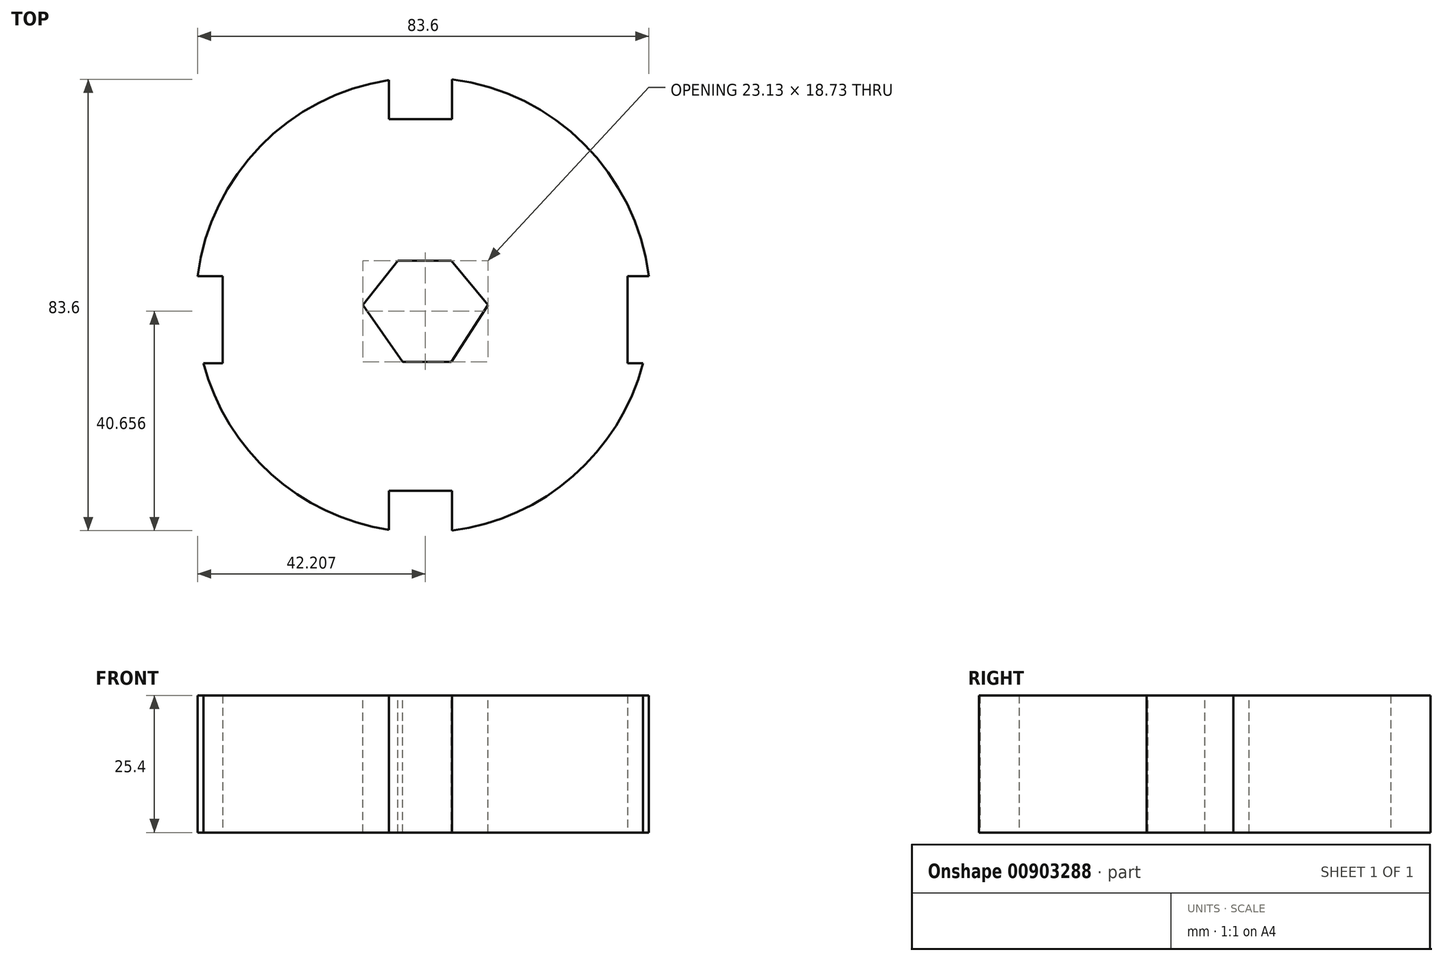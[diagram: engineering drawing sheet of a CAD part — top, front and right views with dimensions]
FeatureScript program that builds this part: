
annotation { "Feature Type Name" : "Feature", "Feature Type Description" : "" }
export const myFeature = defineFeature(function(context is Context, id is Id, definition is map)
    precondition{}
    {
        {
            var Q0;
            Q0=qCreatedBy(makeId("Top.planeOp"),FACE);
            var sketch = newSketch(context, id + "F0", { "sketchPlane" : qUnion([Q0])});
            skCircle(sketch, "E0", {"center": v(0, 0) * mm, "radius": 42.14 * mm});
            skLineSegment(sketch, "E1.bottom", {"start": v(-46.4, 5.32) * mm, "end": v(-37.16, 5.32) * mm});
            skLineSegment(sketch, "E1.top", {"start": v(-46.4, -10.79) * mm, "end": v(-37.16, -10.79) * mm});
            skLineSegment(sketch, "E1.left", {"start": v(-46.4, 5.32) * mm, "end": v(-46.4, -10.79) * mm});
            skLineSegment(sketch, "E1.right", {"start": v(-37.16, 5.32) * mm, "end": v(-37.16, -10.79) * mm});
            skLineSegment(sketch, "E2.bottom", {"start": v(37.87, 5.32) * mm, "end": v(47.11, 5.32) * mm});
            skLineSegment(sketch, "E2.top", {"start": v(37.87, -10.79) * mm, "end": v(47.11, -10.79) * mm});
            skLineSegment(sketch, "E2.left", {"start": v(37.87, 5.32) * mm, "end": v(37.87, -10.79) * mm});
            skLineSegment(sketch, "E2.right", {"start": v(47.11, 5.32) * mm, "end": v(47.11, -10.79) * mm});
            skLineSegment(sketch, "E3", {"start": v(0, 42.14) * mm, "end": v(0, -42.14) * mm, "construction": true});
            skLineSegment(sketch, "E4.MirrorCS", {"start": v(-46.4, -10.79) * mm, "end": v(-46.4, 5.32) * mm});
            skLineSegment(sketch, "E5.bottom", {"start": v(-6.34, 46.75) * mm, "end": v(5.3, 46.75) * mm});
            skLineSegment(sketch, "E5.top", {"start": v(-6.34, 34.42) * mm, "end": v(5.3, 34.42) * mm});
            skLineSegment(sketch, "E5.left", {"start": v(-6.34, 46.75) * mm, "end": v(-6.34, 34.42) * mm});
            skLineSegment(sketch, "E5.right", {"start": v(5.3, 46.75) * mm, "end": v(5.3, 34.42) * mm});
            skLineSegment(sketch, "E6", {"start": v(-42.14, 0) * mm, "end": v(42.14, 0) * mm, "construction": true});
            skLineSegment(sketch, "E7.MirrorCS", {"start": v(-6.34, -34.42) * mm, "end": v(5.3, -34.42) * mm});
            skLineSegment(sketch, "E8.MirrorCS", {"start": v(-6.34, -46.75) * mm, "end": v(-6.34, -34.42) * mm});
            skLineSegment(sketch, "E9.MirrorCS", {"start": v(-6.34, -46.75) * mm, "end": v(5.3, -46.75) * mm});
            skLineSegment(sketch, "E10.MirrorCS", {"start": v(5.3, -46.75) * mm, "end": v(5.3, -34.42) * mm});
            skSolve(sketch);
        }
        {
            var Q0;
            {var subQ0=sQuery(id+"F0.wireOp",EDGE,"E1.right");Q0=makeQuery(id+"F0.imprint","IMPRINT",FACE,{"disambiguationData":[TD([[makeQuery(id+"F0.imprint","IMPRINT",EDGE,{"derivedFrom":subQ0}),1.0]])]});}
            extrude(context, id + "F1", {"entities" : qUnion([Q0]), "depth" : 25.4 * mm, "offsetDistance" : 25.4 * mm});
        }
        {
            var Q0;
            Q0=makeQuery(id+"F1.opExtrude","CAP_FACE",FACE,{"disambiguationData":[OSD([sQuery(id+"F0.wireOp",EDGE,"E0"),sQuery(id+"F0.wireOp",EDGE,"E1.bottom"),sQuery(id+"F0.wireOp",EDGE,"E1.top"),sQuery(id+"F0.wireOp",EDGE,"E1.right"),sQuery(id+"F0.wireOp",EDGE,"E2.bottom"),sQuery(id+"F0.wireOp",EDGE,"E2.top"),sQuery(id+"F0.wireOp",EDGE,"E2.left"),sQuery(id+"F0.wireOp",EDGE,"E5.top"),sQuery(id+"F0.wireOp",EDGE,"E5.left"),sQuery(id+"F0.wireOp",EDGE,"E5.right"),sQuery(id+"F0.wireOp",EDGE,"E7.MirrorCS"),sQuery(id+"F0.wireOp",EDGE,"E8.MirrorCS"),sQuery(id+"F0.wireOp",EDGE,"E10.MirrorCS")])],"isStart":false});
            var sketch = newSketch(context, id + "F2", { "sketchPlane" : qUnion([Q0])});
            skLineSegment(sketch, "E11", {"start": v(-11.16, 0) * mm, "end": v(-4.73, 8.22) * mm});
            skLineSegment(sketch, "E12", {"start": v(-4.73, 8.22) * mm, "end": v(5.22, 8.22) * mm});
            skLineSegment(sketch, "E13", {"start": v(5.22, 8.22) * mm, "end": v(11.97, 0) * mm});
            skLineSegment(sketch, "E14", {"start": v(11.97, 0) * mm, "end": v(5.22, -10.51) * mm});
            skLineSegment(sketch, "E15", {"start": v(5.22, -10.51) * mm, "end": v(-3.8, -10.51) * mm});
            skLineSegment(sketch, "E16", {"start": v(-3.8, -10.51) * mm, "end": v(-11.16, 0) * mm});
            skSolve(sketch);
        }
        {
            var Q0;
            Q0=makeQuery(id+"F2.imprint","IMPRINT",FACE,{"disambiguationData":[TD([[makeQuery(id+"F2.imprint","IMPRINT",EDGE,{"derivedFrom":sQuery(id+"F2.wireOp",EDGE,"E11")}),-1.0]])]});
            extrude(context, id + "F3", {"entities" : qUnion([Q0]), "operationType" : NewBodyOperationType.REMOVE, "oppositeDirection" : true, "depth" : 25.4 * mm, "offsetDistance" : 25.4 * mm});
        }
    });
